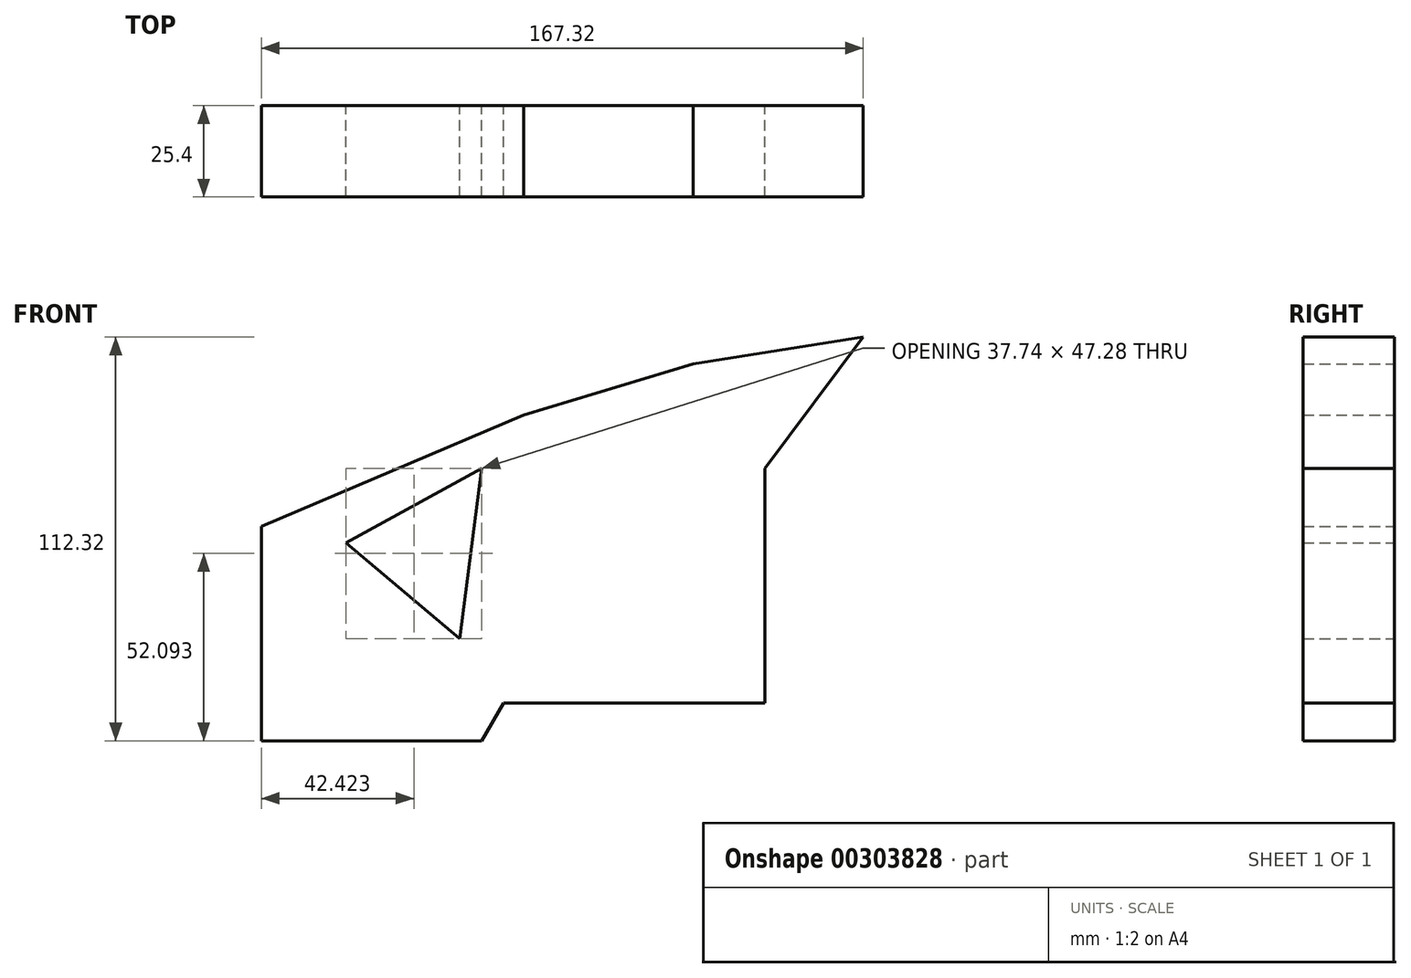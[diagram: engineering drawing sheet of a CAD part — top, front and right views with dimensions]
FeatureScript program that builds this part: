
annotation { "Feature Type Name" : "Feature", "Feature Type Description" : "" }
export const myFeature = defineFeature(function(context is Context, id is Id, definition is map)
    precondition{}
    {
        {
            var Q0;
            Q0=qCreatedBy(makeId("Front.planeOp"),FACE);
            var sketch = newSketch(context, id + "F0", { "sketchPlane" : qUnion([Q0])});
            skLineSegment(sketch, "E0", {"start": v(-82.13, -49.15) * mm, "end": v(-134.84, -49.15) * mm});
            skLineSegment(sketch, "E1", {"start": v(-134.84, -49.15) * mm, "end": v(-143.8, -14.35) * mm});
            skLineSegment(sketch, "E2", {"start": v(-143.8, -14.35) * mm, "end": v(-88.26, 16.04) * mm});
            skLineSegment(sketch, "E3", {"start": v(-88.26, 16.04) * mm, "end": v(-76.61, 30.9) * mm});
            skLineSegment(sketch, "E4", {"start": v(-76.61, 30.9) * mm, "end": v(-149.55, 0) * mm});
            skLineSegment(sketch, "E5", {"start": v(-149.55, 0) * mm, "end": v(-149.55, -59.69) * mm});
            skLineSegment(sketch, "E6", {"start": v(-149.55, -59.69) * mm, "end": v(-88.26, -59.69) * mm});
            skLineSegment(sketch, "E7", {"start": v(-88.26, -59.69) * mm, "end": v(-82.13, -49.15) * mm});
            skLineSegment(sketch, "E8", {"start": v(-76.61, 30.9) * mm, "end": v(-29.42, 45.13) * mm});
            skLineSegment(sketch, "E9", {"start": v(-29.42, 45.13) * mm, "end": v(17.77, 52.63) * mm});
            skLineSegment(sketch, "E10", {"start": v(17.77, 52.63) * mm, "end": v(-9.55, 16.04) * mm});
            skLineSegment(sketch, "E11", {"start": v(-9.55, 16.04) * mm, "end": v(-88.26, 16.04) * mm});
            skLineSegment(sketch, "E12", {"start": v(-9.55, 16.04) * mm, "end": v(-9.55, -49.15) * mm});
            skLineSegment(sketch, "E13", {"start": v(-9.55, -49.15) * mm, "end": v(-82.13, -49.15) * mm});
            skLineSegment(sketch, "E14", {"start": v(-126, -4.6) * mm, "end": v(-94.39, -31.23) * mm});
            skLineSegment(sketch, "E15", {"start": v(-94.39, -31.23) * mm, "end": v(-88.26, 16.04) * mm});
            skLineSegment(sketch, "E16", {"start": v(22.68, 52.63) * mm, "end": v(22.68, -31.23) * mm});
            skLineSegment(sketch, "E17", {"start": v(22.68, -31.23) * mm, "end": v(-9.55, -49.15) * mm});
            skSolve(sketch);
        }
        {
            var Q0;
            Q0 = qSketchRegion(id + "F0", true);
            extrude(context, id + "F1", {"entities" : qUnion([Q0]), "depth" : 25.4 * mm});
        }
    });
